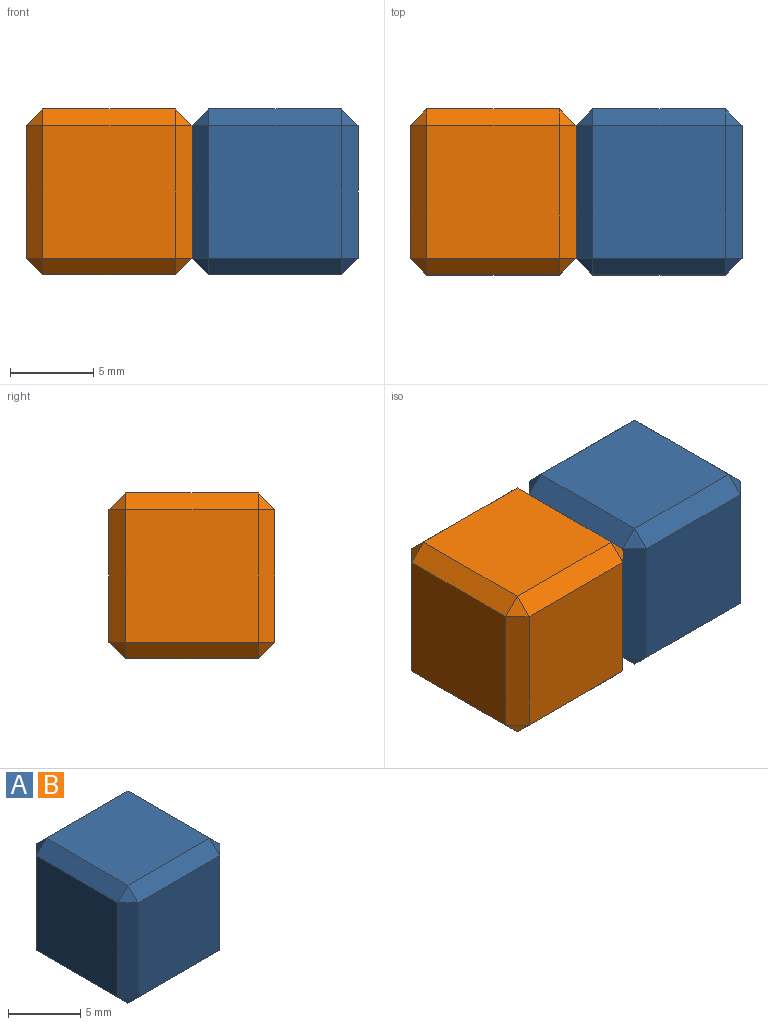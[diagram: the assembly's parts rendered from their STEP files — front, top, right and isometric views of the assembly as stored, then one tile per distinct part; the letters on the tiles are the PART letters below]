
ASSEMBLY  parts=2 mates=1
PART A: 26 faces, bbox 10x10x10 mm
  f0: plane 8x8mm, normal (1,0,0), area 64mm2, adj f11,f20,f21,f25
  f1: plane 8x8mm, normal (0,1,0), area 64mm2, adj f6,f10,f11,f12
  f2: plane 8x8mm, normal (-1,0,0), area 64mm2, adj f6,f9,f13,f14
  f3: plane 8x8mm, normal (0,-1,0), area 64mm2, adj f14,f19,f22,f25
  f4: plane 8x8mm, normal (0,0,1), area 64mm2, adj f9,f10,f19,f20
  f5: plane 8x8mm, normal (0,0,-1), area 64mm2, adj f12,f13,f21,f22
  f6: plane 8x1mm, normal (-0.71,0.71,0), area 11.3mm2, adj f1,f2,f7,f8
  f7: plane 1x1mm, normal (-0.58,0.58,0.58), area 0.9mm2, adj f6,f9,f10
  f8: plane 1x1mm, normal (-0.58,0.58,-0.58), area 0.9mm2, adj f6,f12,f13
  f9: plane 8x1mm, normal (-0.71,0,0.71), area 11.3mm2, adj f2,f4,f7,f15
  f10: plane 8x1mm, normal (0,0.71,0.71), area 11.3mm2, adj f1,f4,f7,f16
  f11: plane 8x1mm, normal (0.71,0.71,0), area 11.3mm2, adj f0,f1,f16,f17
  f12: plane 8x1mm, normal (0,0.71,-0.71), area 11.3mm2, adj f1,f5,f8,f17
  f13: plane 8x1mm, normal (-0.71,0,-0.71), area 11.3mm2, adj f2,f5,f8,f18
  f14: plane 8x1mm, normal (-0.71,-0.71,0), area 11.3mm2, adj f2,f3,f15,f18
  f15: plane 1x1mm, normal (-0.58,-0.58,0.58), area 0.9mm2, adj f9,f14,f19
  f16: plane 1x1mm, normal (0.58,0.58,0.58), area 0.9mm2, adj f10,f11,f20
  f17: plane 1x1mm, normal (0.58,0.58,-0.58), area 0.9mm2, adj f11,f12,f21
  f18: plane 1x1mm, normal (-0.58,-0.58,-0.58), area 0.9mm2, adj f13,f14,f22
  f19: plane 8x1mm, normal (0,-0.71,0.71), area 11.3mm2, adj f3,f4,f15,f23
  f20: plane 8x1mm, normal (0.71,0,0.71), area 11.3mm2, adj f0,f4,f16,f23
  f21: plane 8x1mm, normal (0.71,0,-0.71), area 11.3mm2, adj f0,f5,f17,f24
  f22: plane 8x1mm, normal (0,-0.71,-0.71), area 11.3mm2, adj f3,f5,f18,f24
  f23: plane 1x1mm, normal (0.58,-0.58,0.58), area 0.9mm2, adj f19,f20,f25
  f24: plane 1x1mm, normal (0.58,-0.58,-0.58), area 0.9mm2, adj f21,f22,f25
  f25: plane 8x1mm, normal (0.71,-0.71,0), area 11.3mm2, adj f0,f3,f23,f24
PART B: same geometry as A
PLACE A t=(4.29,3.91,-2.85)mm
PLACE B t=(-5.71,3.91,-2.85)mm
MATE fastened B.f0 <-> A.f2  axis (1,0,0) through (-0.71,3.91,2.15)mm
